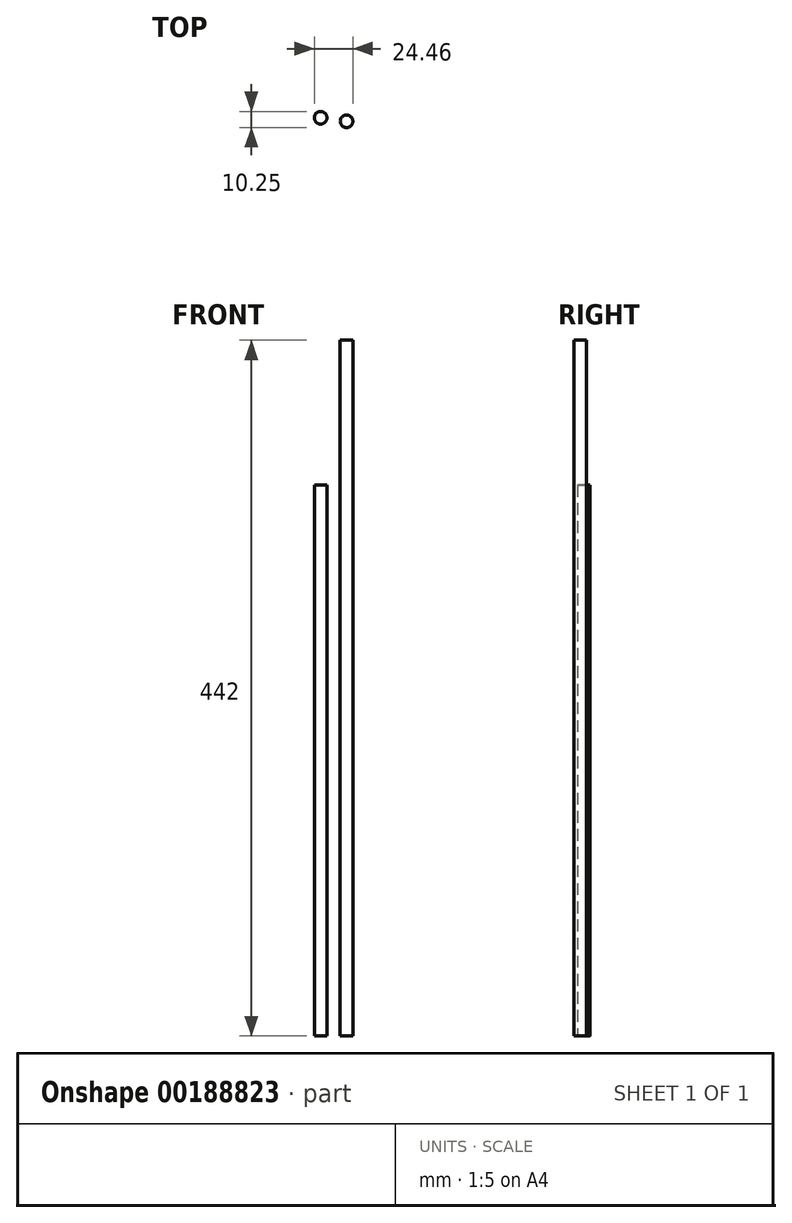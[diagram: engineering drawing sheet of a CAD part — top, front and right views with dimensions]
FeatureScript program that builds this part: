
annotation { "Feature Type Name" : "Feature", "Feature Type Description" : "" }
export const myFeature = defineFeature(function(context is Context, id is Id, definition is map)
    precondition{}
    {
        {
            var Q0;
            Q0=qCreatedBy(makeId("Top.planeOp"),FACE);
            var sketch = newSketch(context, id + "F0", { "sketchPlane" : qUnion([Q0])});
            skCircle(sketch, "E0", {"center": v(0, 0) * mm, "radius": 4 * mm});
            skCircle(sketch, "E1", {"center": v(16.46, -2.25) * mm, "radius": 4 * mm});
            skSolve(sketch);
        }
        {
            var Q0;
            Q0=makeQuery(id+"F0.imprint","IMPRINT",FACE,{"disambiguationData":[TD([[makeQuery(id+"F0.imprint","IMPRINT",EDGE,{"derivedFrom":sQuery(id+"F0.wireOp",EDGE,"E0")}),1.0]])]});
            extrude(context, id + "F1", {"entities" : qUnion([Q0]), "depth" : 350 * mm});
        }
        {
            var Q0;
            Q0=makeQuery(id+"F0.imprint","IMPRINT",FACE,{"disambiguationData":[TD([[makeQuery(id+"F0.imprint","IMPRINT",EDGE,{"derivedFrom":sQuery(id+"F0.wireOp",EDGE,"E1")}),1.0]])]});
            var Q1;
            Q1=sQuery(id+"F0.wireOp",EDGE,"E1");
            extrude(context, id + "F2", {"entities" : qUnion([Q0]), "surfaceEntities" : qUnion([Q1]), "depth" : (465 - 23) * mm, "offsetDistance" : 25 * mm});
        }
    });
